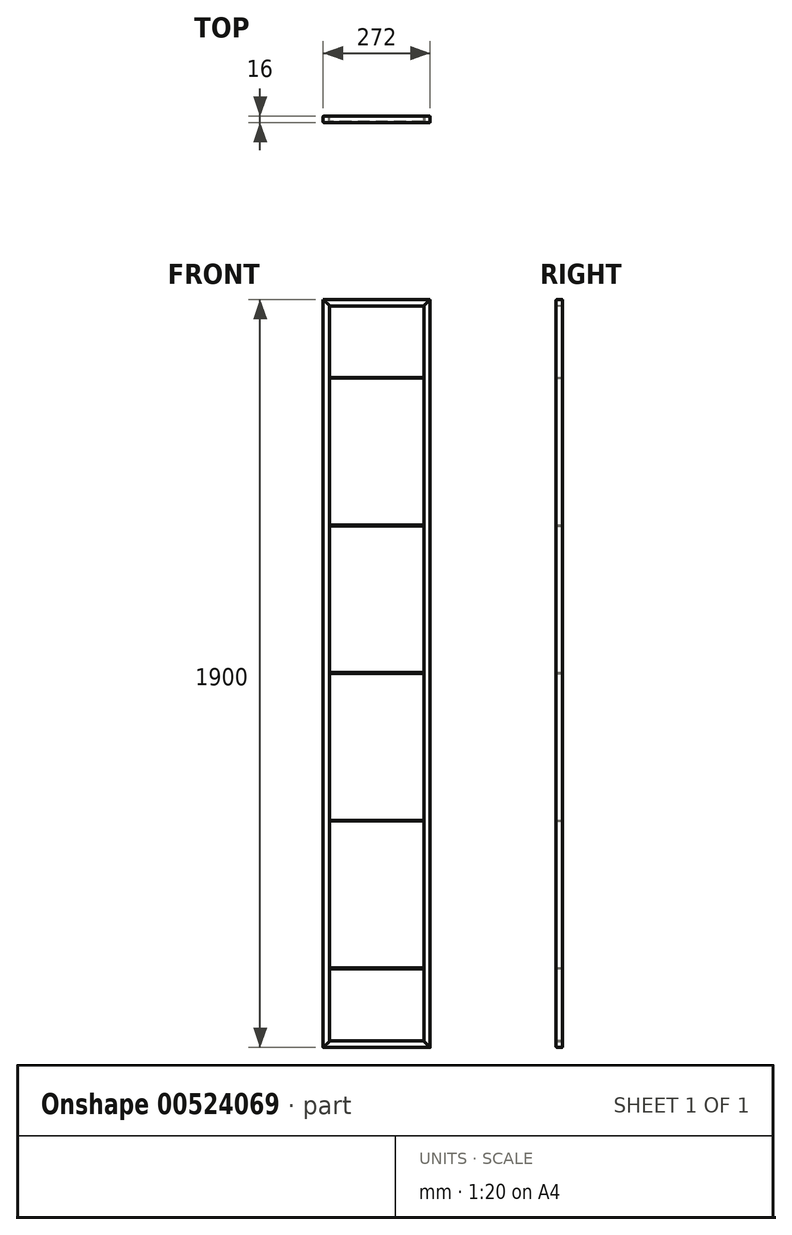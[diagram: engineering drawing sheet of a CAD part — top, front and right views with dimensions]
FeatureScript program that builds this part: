
annotation { "Feature Type Name" : "Feature", "Feature Type Description" : "" }
export const myFeature = defineFeature(function(context is Context, id is Id, definition is map)
    precondition{}
    {
        {
            assignVariable(context, id + "F0", {"name" : "B", "anyValue" : 16});
        }
        {
            assignVariable(context, id + "F1", {"name" : "W", "anyValue" : 1});
        }
        {
            assignVariable(context, id + "F2", {"name" : "R", "anyValue" : 1.5});
        }
        {
            assignVariable(context, id + "F3", {"name" : "H", "anyValue" : 1900});
        }
        {
            assignVariable(context, id + "F4", {"name" : "D", "anyValue" : 240});
        }
        {
            var Q0;
            Q0=qCreatedBy(makeId("Top.planeOp"),FACE);
            var sketch = newSketch(context, id + "F5", { "sketchPlane" : qUnion([Q0])});
            skLineSegment(sketch, "E0.bottom", {"start": v(-136, 8) * mm, "end": v(-120, 8) * mm});
            skLineSegment(sketch, "E0.top", {"start": v(-136, -8) * mm, "end": v(-120, -8) * mm});
            skLineSegment(sketch, "E0.left", {"start": v(-136, 8) * mm, "end": v(-136, -8) * mm});
            skLineSegment(sketch, "E0.right", {"start": v(-120, 8) * mm, "end": v(-120, -8) * mm});
            skSolve(sketch);
        }
        {
            var Q0;
            Q0 = qSketchRegion(id + "F5", true);
            extrude(context, id + "F6", {"entities" : qUnion([Q0]), "endBound" : BoundingType.SYMMETRIC, "depth" : (getVariable(context, 'H')) * mm, "offsetDistance" : 25 * mm});
        }
        {
            var Q0;
            Q0=makeQuery(id+"F6.opExtrude","SWEPT_EDGE",EDGE,{"disambiguationData":[OSD([sQuery(id+"F5.wireOp",EDGE,"E0.top"),sQuery(id+"F5.wireOp",EDGE,"E0.right")])]});
            var Q1;
            Q1=makeQuery(id+"F6.opExtrude","SWEPT_EDGE",EDGE,{"disambiguationData":[OSD([sQuery(id+"F5.wireOp",EDGE,"E0.bottom"),sQuery(id+"F5.wireOp",EDGE,"E0.right")])]});
            var Q2;
            Q2=makeQuery(id+"F6.opExtrude","SWEPT_EDGE",EDGE,{"disambiguationData":[OSD([sQuery(id+"F5.wireOp",EDGE,"E0.bottom"),sQuery(id+"F5.wireOp",EDGE,"E0.left")])]});
            var Q3;
            Q3=makeQuery(id+"F6.opExtrude","SWEPT_EDGE",EDGE,{"disambiguationData":[OSD([sQuery(id+"F5.wireOp",EDGE,"E0.top"),sQuery(id+"F5.wireOp",EDGE,"E0.left")])]});
            fillet(context, id + "F7", {"entities" : qUnion([Q0, Q1, Q2, Q3]), "radius" : (getVariable(context, 'R')) * mm, "tangentPropagation" : true, "allowEdgeOverflow" : false});
        }
        {
            var Q0;
            Q0=makeQuery(id+"F6.opExtrude","CAP_FACE",FACE,{"disambiguationData":[OSD([sQuery(id+"F5.wireOp",EDGE,"E0.bottom"),sQuery(id+"F5.wireOp",EDGE,"E0.top"),sQuery(id+"F5.wireOp",EDGE,"E0.left"),sQuery(id+"F5.wireOp",EDGE,"E0.right")])],"isStart":false});
            var Q1;
            Q1=makeQuery(id+"F6.opExtrude","CAP_FACE",FACE,{"disambiguationData":[OSD([sQuery(id+"F5.wireOp",EDGE,"E0.bottom"),sQuery(id+"F5.wireOp",EDGE,"E0.top"),sQuery(id+"F5.wireOp",EDGE,"E0.left"),sQuery(id+"F5.wireOp",EDGE,"E0.right")])],"isStart":true});
            shell(context, id + "F8", {"entities" : qUnion([Q0, Q1]), "thickness" : (getVariable(context, 'W')) * mm});
        }
        {
            var Q0;
            Q0=makeQuery(id+"F6.opExtrude","SWEPT_FACE",FACE,{"disambiguationData":[OSD([sQuery(id+"F5.wireOp",EDGE,"E0.top")])]});
            var sketch = newSketch(context, id + "F9", { "sketchPlane" : qUnion([Q0])});
            skLineSegment(sketch, "E1.0", {"start": v(-136, -950) * mm, "end": v(-136, 950) * mm, "construction": true});
            skLineSegment(sketch, "E1.1", {"start": v(-120, 950) * mm, "end": v(-120, -950) * mm, "construction": true});
            skLineSegment(sketch, "E2", {"start": v(-136, 950) * mm, "end": v(-120, 934) * mm});
            skLineSegment(sketch, "E3", {"start": v(-120, 934) * mm, "end": v(-120, 950) * mm});
            skLineSegment(sketch, "E4", {"start": v(-136, 950) * mm, "end": v(-120, 950) * mm});
            skLineSegment(sketch, "E5", {"start": v(-136, -950) * mm, "end": v(-120, -934) * mm});
            skLineSegment(sketch, "E6", {"start": v(-120, -934) * mm, "end": v(-120, -950) * mm});
            skLineSegment(sketch, "E7", {"start": v(-136, -950) * mm, "end": v(-120, -950) * mm});
            skSolve(sketch);
        }
        {
            var Q0;
            Q0 = qSketchRegion(id + "F9", true);
            extrude(context, id + "F10", {"entities" : qUnion([Q0]), "operationType" : NewBodyOperationType.REMOVE, "endBound" : BoundingType.THROUGH_ALL, "oppositeDirection" : true, "depth" : 25 * mm, "offsetDistance" : 25 * mm});
        }
        {
            var Q0;
            Q0=makeQuery(id+"F6.opExtrude","SWEPT_FACE",FACE,{"disambiguationData":[OSD([sQuery(id+"F5.wireOp",EDGE,"E0.top")])]});
            var sketch = newSketch(context, id + "F11", { "sketchPlane" : qUnion([Q0])});
            skLineSegment(sketch, "E8.0", {"start": v(-136, -950) * mm, "end": v(-136, 950) * mm, "construction": true});
            skLineSegment(sketch, "E9.0", {"start": v(-120, 934) * mm, "end": v(-120, -934) * mm, "construction": true});
            skLineSegment(sketch, "E10", {"start": v(-136, 950) * mm, "end": v(136, 950) * mm});
            skLineSegment(sketch, "E11", {"start": v(136, 950) * mm, "end": v(120, 934) * mm});
            skLineSegment(sketch, "E12", {"start": v(120, 934) * mm, "end": v(-120, 934) * mm});
            skLineSegment(sketch, "E13", {"start": v(-136, 950) * mm, "end": v(-120, 934) * mm});
            skSolve(sketch);
        }
        {
            var Q0;
            Q0 = qSketchRegion(id + "F11", true);
            extrude(context, id + "F12", {"entities" : qUnion([Q0]), "oppositeDirection" : true, "depth" : (getVariable(context, 'B')) * mm, "offsetDistance" : 25 * mm});
        }
        {
            var Q0;
            Q0=makeQuery(id+"F12.opExtrude","CAP_EDGE",EDGE,{"disambiguationData":[OSD([sQuery(id+"F11.wireOp",EDGE,"E10")])],"isStart":true});
            var Q1;
            Q1=makeQuery(id+"F12.opExtrude","CAP_EDGE",EDGE,{"disambiguationData":[OSD([sQuery(id+"F11.wireOp",EDGE,"E12")])],"isStart":true});
            var Q2;
            Q2=makeQuery(id+"F12.opExtrude","CAP_EDGE",EDGE,{"disambiguationData":[OSD([sQuery(id+"F11.wireOp",EDGE,"E12")])],"isStart":false});
            var Q3;
            Q3=makeQuery(id+"F12.opExtrude","CAP_EDGE",EDGE,{"disambiguationData":[OSD([sQuery(id+"F11.wireOp",EDGE,"E10")])],"isStart":false});
            fillet(context, id + "F13", {"entities" : qUnion([Q0, Q1, Q2, Q3]), "radius" : (getVariable(context, 'R')) * mm, "tangentPropagation" : true, "allowEdgeOverflow" : false});
        }
        {
            var Q0;
            Q0=makeQuery(id+"F12.opExtrude","SWEPT_FACE",FACE,{"disambiguationData":[OSD([sQuery(id+"F11.wireOp",EDGE,"E11")])]});
            var Q1;
            Q1=makeQuery(id+"F12.opExtrude","SWEPT_FACE",FACE,{"disambiguationData":[OSD([sQuery(id+"F11.wireOp",EDGE,"E13")])]});
            shell(context, id + "F14", {"entities" : qUnion([Q0, Q1]), "thickness" : (getVariable(context, 'W')) * mm});
        }
        {
            var Q0;
            Q0=makeQuery(id+"F6.opExtrude","SWEPT_BODY",BODY,{"disambiguationData":[OSD([sQuery(id+"F5.wireOp",EDGE,"E0.bottom"),sQuery(id+"F5.wireOp",EDGE,"E0.top"),sQuery(id+"F5.wireOp",EDGE,"E0.left"),sQuery(id+"F5.wireOp",EDGE,"E0.right")])]});
            var Q1;
            Q1=qCreatedBy(makeId("Right.planeOp"),FACE);
            mirror(context, id + "F15", {"entities" : qUnion([Q0]), "mirrorPlane" : qUnion([Q1])});
        }
        {
            var Q0;
            Q0=makeQuery(id+"F12.opExtrude","SWEPT_BODY",BODY,{"disambiguationData":[OSD([sQuery(id+"F11.wireOp",EDGE,"E10"),sQuery(id+"F11.wireOp",EDGE,"E11"),sQuery(id+"F11.wireOp",EDGE,"E12"),sQuery(id+"F11.wireOp",EDGE,"E13")])]});
            var Q1;
            Q1=qCreatedBy(makeId("Top.planeOp"),FACE);
            mirror(context, id + "F16", {"entities" : qUnion([Q0]), "mirrorPlane" : qUnion([Q1])});
        }
        {
            var Q0;
            Q0=makeQuery(id+"F6.opExtrude","SWEPT_FACE",FACE,{"disambiguationData":[OSD([sQuery(id+"F5.wireOp",EDGE,"E0.right")])]});
            var sketch = newSketch(context, id + "F17", { "sketchPlane" : qUnion([Q0])});
            skLineSegment(sketch, "E14", {"start": v(-6.5, -748) * mm, "end": v(6.5, -748) * mm});
            skLineSegment(sketch, "E15", {"start": v(6.5, -748) * mm, "end": v(6.5, -750) * mm});
            skLineSegment(sketch, "E16", {"start": v(6.5, -750) * mm, "end": v(-6.5, -750) * mm});
            skLineSegment(sketch, "E17", {"start": v(-6.5, -750) * mm, "end": v(-6.5, -748) * mm});
            skLineSegment(sketch, "E18.bottom", {"start": v(-6.5, 752) * mm, "end": v(6.5, 752) * mm});
            skLineSegment(sketch, "E18.top", {"start": v(-6.5, 750) * mm, "end": v(6.5, 750) * mm});
            skLineSegment(sketch, "E18.left", {"start": v(-6.5, 752) * mm, "end": v(-6.5, 750) * mm});
            skLineSegment(sketch, "E18.right", {"start": v(6.5, 752) * mm, "end": v(6.5, 750) * mm});
            skLineSegment(sketch, "E19.bottom", {"start": v(-6.5, 377) * mm, "end": v(6.5, 377) * mm});
            skLineSegment(sketch, "E19.top", {"start": v(-6.5, 375) * mm, "end": v(6.5, 375) * mm});
            skLineSegment(sketch, "E19.left", {"start": v(-6.5, 377) * mm, "end": v(-6.5, 375) * mm});
            skLineSegment(sketch, "E19.right", {"start": v(6.5, 377) * mm, "end": v(6.5, 375) * mm});
            skLineSegment(sketch, "E20.bottom", {"start": v(-6.5, 2) * mm, "end": v(6.5, 2) * mm});
            skLineSegment(sketch, "E20.top", {"start": v(-6.5, 0) * mm, "end": v(6.5, 0) * mm});
            skLineSegment(sketch, "E20.left", {"start": v(-6.5, 2) * mm, "end": v(-6.5, 0) * mm});
            skLineSegment(sketch, "E20.right", {"start": v(6.5, 2) * mm, "end": v(6.5, 0) * mm});
            skLineSegment(sketch, "E21.bottom", {"start": v(-6.5, -373) * mm, "end": v(6.5, -373) * mm});
            skLineSegment(sketch, "E21.top", {"start": v(-6.5, -375) * mm, "end": v(6.5, -375) * mm});
            skLineSegment(sketch, "E21.left", {"start": v(-6.5, -373) * mm, "end": v(-6.5, -375) * mm});
            skLineSegment(sketch, "E21.right", {"start": v(6.5, -373) * mm, "end": v(6.5, -375) * mm});
            skSolve(sketch);
        }
        {
            var Q0;
            Q0 = qSketchRegion(id + "F17", true);
            extrude(context, id + "F18", {"entities" : qUnion([Q0]), "depth" : (getVariable(context, 'D')) * mm, "offsetDistance" : 25 * mm});
        }
    });
